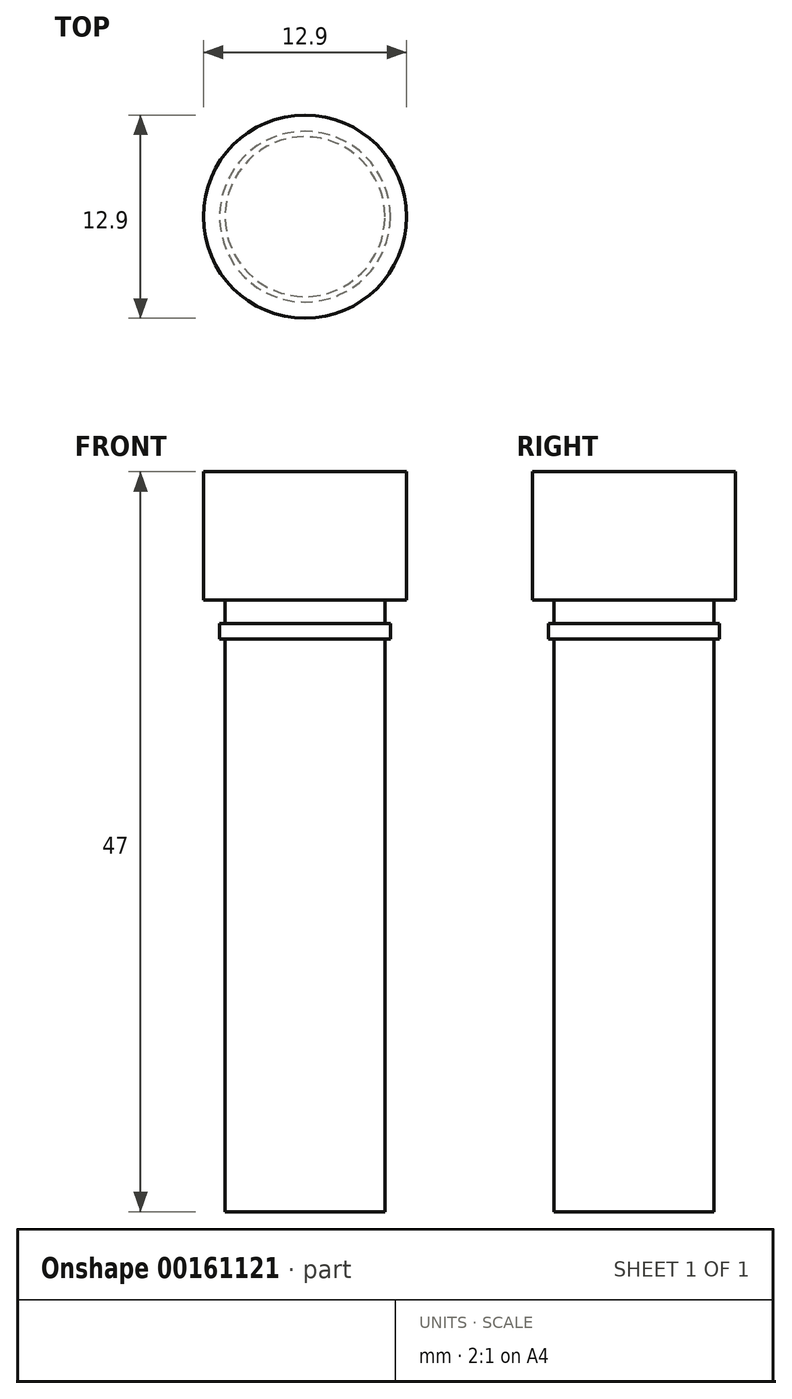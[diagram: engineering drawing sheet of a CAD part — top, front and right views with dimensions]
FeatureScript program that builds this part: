
annotation { "Feature Type Name" : "Feature", "Feature Type Description" : "" }
export const myFeature = defineFeature(function(context is Context, id is Id, definition is map)
    precondition{}
    {
        {
            var Q0;
            Q0=qCreatedBy(makeId("Front.planeOp"),FACE);
            var sketch = newSketch(context, id + "F0", { "sketchPlane" : qUnion([Q0])});
            skLineSegment(sketch, "E0", {"start": v(0, 0) * mm, "end": v(0, 47) * mm});
            skLineSegment(sketch, "E1", {"start": v(5.08, 0) * mm, "end": v(5.08, 36.37) * mm});
            skLineSegment(sketch, "E2", {"start": v(5.08, 0) * mm, "end": v(0, 0) * mm});
            skLineSegment(sketch, "E3", {"start": v(5.08, 36.37) * mm, "end": v(5.42, 36.37) * mm});
            skLineSegment(sketch, "E4", {"start": v(5.42, 36.37) * mm, "end": v(5.42, 37.37) * mm});
            skLineSegment(sketch, "E5", {"start": v(5.42, 37.37) * mm, "end": v(5.08, 37.37) * mm});
            skLineSegment(sketch, "E6", {"start": v(5.08, 37.37) * mm, "end": v(5.08, 38.84) * mm});
            skLineSegment(sketch, "E7", {"start": v(5.08, 38.84) * mm, "end": v(6.45, 38.84) * mm});
            skLineSegment(sketch, "E8", {"start": v(6.45, 38.84) * mm, "end": v(6.45, 47) * mm});
            skLineSegment(sketch, "E9", {"start": v(6.45, 47) * mm, "end": v(0, 47) * mm});
            skSolve(sketch);
        }
        {
            var Q0;
            Q0=makeQuery(id+"F0.imprint","IMPRINT",FACE,{"disambiguationData":[TD([[makeQuery(id+"F0.imprint","IMPRINT",EDGE,{"derivedFrom":sQuery(id+"F0.wireOp",EDGE,"E0")}),-1.0]])]});
            var Q1;
            Q1=qConstructionFilter(qBodyType(qCreatedBy(id+"F0",EDGE),BodyType.WIRE),ConstructionObject.NO);
            var Q2;
            Q2=sQuery(id+"F0.wireOp",EDGE,"E0");
            revolve(context, id + "F1", {"entities" : qUnion([Q0]), "surfaceEntities" : qUnion([Q1]), "axis" : qUnion([Q2]), "revolveType" : RevolveType.FULL});
        }
    });
